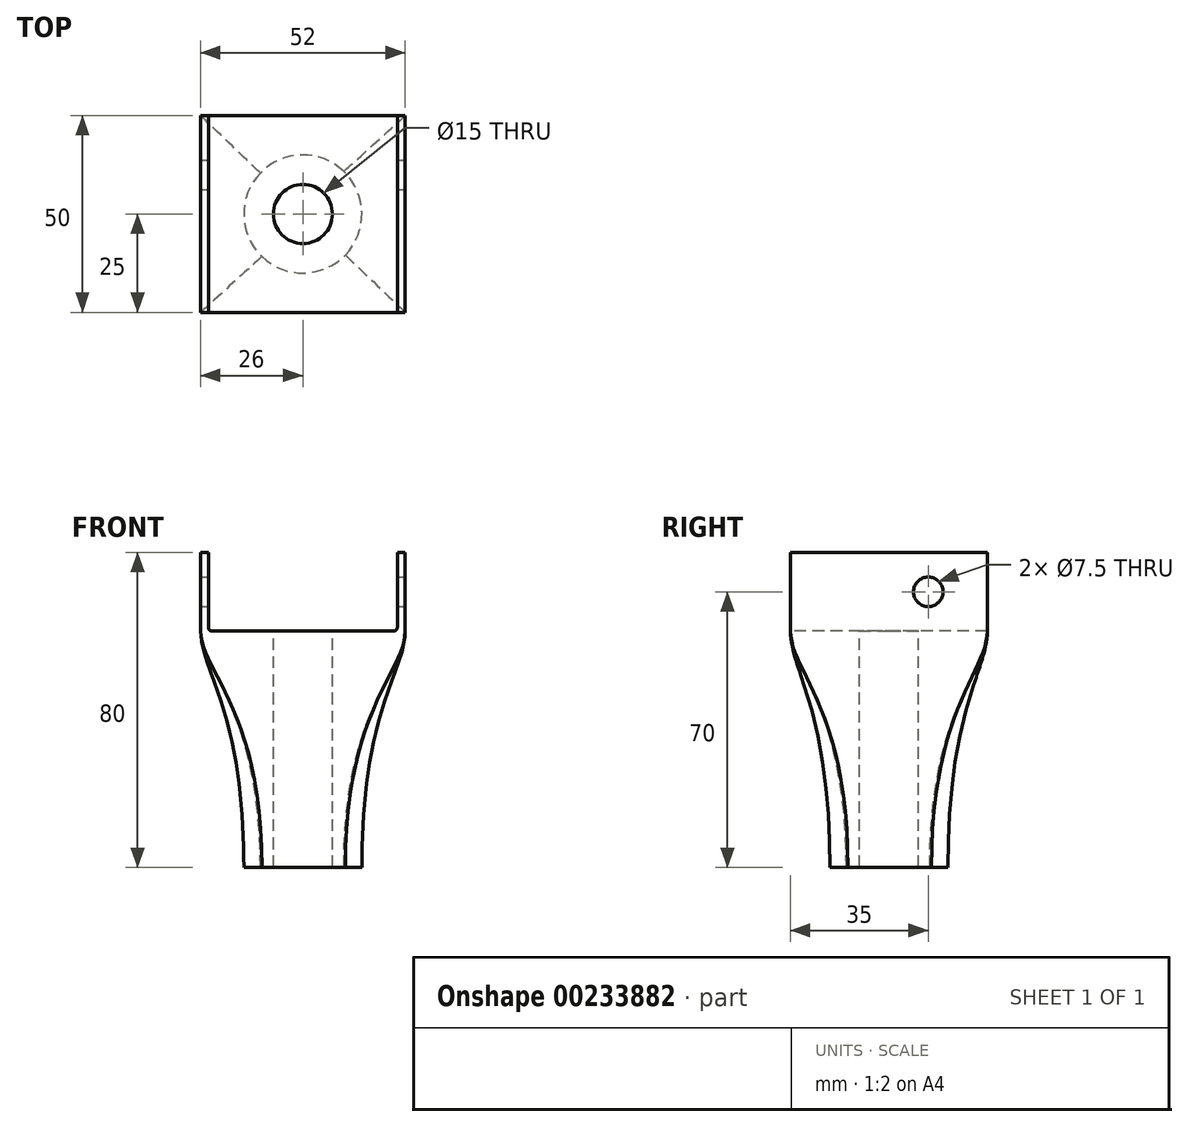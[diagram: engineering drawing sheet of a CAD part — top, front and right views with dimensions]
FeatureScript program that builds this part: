
annotation { "Feature Type Name" : "Feature", "Feature Type Description" : "" }
export const myFeature = defineFeature(function(context is Context, id is Id, definition is map)
    precondition{}
    {
        {
            var Q0;
            Q0=qCreatedBy(makeId("Top.planeOp"),FACE);
            cPlane(context, id + "F0", {"entities" : qUnion([Q0]), "cplaneType" : CPlaneType.OFFSET, "offset" : 60 * mm, "oppositeDirection" : true, "width" : 150 * mm, "height" : 150 * mm});
        }
        {
            var Q0;
            Q0=qCreatedBy(id+"F0.planeOp",FACE);
            var sketch = newSketch(context, id + "F1", { "sketchPlane" : qUnion([Q0])});
            skCircle(sketch, "E0", {"center": v(0, 0) * mm, "radius": 15 * mm});
            skSolve(sketch);
        }
        {
            var Q0;
            Q0=qCreatedBy(makeId("Top.planeOp"),FACE);
            var sketch = newSketch(context, id + "F2", { "sketchPlane" : qUnion([Q0])});
            skLineSegment(sketch, "E1.bottom", {"start": v(26, -25) * mm, "end": v(-26, -25) * mm});
            skLineSegment(sketch, "E1.top", {"start": v(26, 25) * mm, "end": v(-26, 25) * mm});
            skLineSegment(sketch, "E1.left", {"start": v(26, -25) * mm, "end": v(26, 25) * mm});
            skLineSegment(sketch, "E1.right", {"start": v(-26, -25) * mm, "end": v(-26, 25) * mm});
            skPoint(sketch, "E1.middle", {"position": v(0, 0) * mm});
            skSolve(sketch);
        }
        {
            var Q0;
            Q0=makeQuery(id+"F1.imprint","IMPRINT",FACE,{"disambiguationData":[TD([[makeQuery(id+"F1.imprint","IMPRINT",EDGE,{"derivedFrom":sQuery(id+"F1.wireOp",EDGE,"E0")}),1.0]])]});
            var Q1;
            Q1=makeQuery(id+"F2.imprint","IMPRINT",FACE,{"disambiguationData":[TD([[makeQuery(id+"F2.imprint","IMPRINT",EDGE,{"derivedFrom":sQuery(id+"F2.wireOp",EDGE,"E1.bottom")}),-1.0]])]});
            loft(context, id + "F3", {"startCondition" : LoftEndDerivativeType.NORMAL_TO_PROFILE, "startMagnitude" : 2, "endCondition" : LoftEndDerivativeType.NORMAL_TO_PROFILE, "endMagnitude" : 0.5, "sheetProfilesArray" : [{ "sheetProfileEntities" : qUnion([Q0]) }, { "sheetProfileEntities" : qUnion([Q1]) }]});
        }
        {
            var Q0;
            Q0=makeQuery(id+"F3.opLoft","CAP_FACE",FACE,{"disambiguationData":[OSD([makeQuery(id+"F2.imprint","IMPRINT",FACE,{"disambiguationData":[TD([[makeQuery(id+"F2.imprint","IMPRINT",EDGE,{"derivedFrom":sQuery(id+"F2.wireOp",EDGE,"E1.bottom")}),-1.0]])]})])],"isStart":true});
            extrude(context, id + "F4", {"entities" : qUnion([Q0]), "operationType" : NewBodyOperationType.ADD, "depth" : 20 * mm});
        }
        {
            var Q0;
            Q0=qCreatedBy(makeId("Front.planeOp"),FACE);
            var sketch = newSketch(context, id + "F5", { "sketchPlane" : qUnion([Q0])});
            skLineSegment(sketch, "E2.0.1", {"start": v(26, 20) * mm, "end": v(-26, 20) * mm});
            skLineSegment(sketch, "E2.0.3", {"start": v(-26, 20) * mm, "end": v(26, 20) * mm});
            skLineSegment(sketch, "E3.bottom", {"start": v(-24, 0) * mm, "end": v(24, 0) * mm});
            skLineSegment(sketch, "E3.top", {"start": v(-24, 20) * mm, "end": v(24, 20) * mm});
            skLineSegment(sketch, "E3.left", {"start": v(-24, 0) * mm, "end": v(-24, 20) * mm});
            skLineSegment(sketch, "E3.right", {"start": v(24, 0) * mm, "end": v(24, 20) * mm});
            skSolve(sketch);
        }
        {
            var Q0;
            Q0=makeQuery(id+"F5.imprint","IMPRINT",FACE,{"disambiguationData":[TD([[makeQuery(id+"F5.imprint","IMPRINT",EDGE,{"derivedFrom":sQuery(id+"F5.wireOp",EDGE,"E3.bottom")}),1.0]])]});
            extrude(context, id + "F6", {"entities" : qUnion([Q0]), "operationType" : NewBodyOperationType.REMOVE, "endBound" : BoundingType.SYMMETRIC, "oppositeDirection" : true, "depth" : 50 * mm});
        }
        {
            var Q0;
            Q0=qCreatedBy(makeId("Top.planeOp"),FACE);
            var sketch = newSketch(context, id + "F7", { "sketchPlane" : qUnion([Q0])});
            skCircle(sketch, "E4", {"center": v(0, 0) * mm, "radius": 7.5 * mm});
            skSolve(sketch);
        }
        {
            var Q0;
            Q0=makeQuery(id+"F7.imprint","IMPRINT",FACE,{"disambiguationData":[TD([[makeQuery(id+"F7.imprint","IMPRINT",EDGE,{"derivedFrom":sQuery(id+"F7.wireOp",EDGE,"E4")}),1.0]])]});
            extrude(context, id + "F8", {"entities" : qUnion([Q0]), "operationType" : NewBodyOperationType.REMOVE, "endBound" : BoundingType.THROUGH_ALL, "oppositeDirection" : true, "depth" : 50 * mm});
        }
        {
            var Q0;
            Q0=qCreatedBy(makeId("Right.planeOp"),FACE);
            var sketch = newSketch(context, id + "F9", { "sketchPlane" : qUnion([Q0])});
            skCircle(sketch, "E5", {"center": v(10, 10) * mm, "radius": 3.75 * mm});
            skSolve(sketch);
        }
        {
            var Q0;
            Q0=makeQuery(id+"F9.imprint","IMPRINT",FACE,{"disambiguationData":[TD([[makeQuery(id+"F9.imprint","IMPRINT",EDGE,{"derivedFrom":sQuery(id+"F9.wireOp",EDGE,"E5")}),1.0]])]});
            extrude(context, id + "F10", {"entities" : qUnion([Q0]), "operationType" : NewBodyOperationType.REMOVE, "endBound" : BoundingType.SYMMETRIC, "oppositeDirection" : true, "depth" : 100 * mm});
        }
        {
            var Q0;
            Q0=makeQuery(id+"F6.boolean.opBoolean","COPY",EDGE,{"derivedFrom":makeQuery(id+"F6.opExtrude","SWEPT_EDGE",EDGE,{"disambiguationData":[OSD([sQuery(id+"F5.wireOp",EDGE,"E3.bottom"),sQuery(id+"F5.wireOp",EDGE,"E3.left")])]})});
            var Q1;
            Q1=makeQuery(id+"F6.boolean.opBoolean","COPY",EDGE,{"derivedFrom":makeQuery(id+"F6.opExtrude","SWEPT_EDGE",EDGE,{"disambiguationData":[OSD([sQuery(id+"F5.wireOp",EDGE,"E3.bottom"),sQuery(id+"F5.wireOp",EDGE,"E3.right")])]})});
            fillet(context, id + "F11", {"entities" : qUnion([Q0, Q1]), "radius" : 1 * mm, "tangentPropagation" : true, "allowEdgeOverflow" : false});
        }
    });
